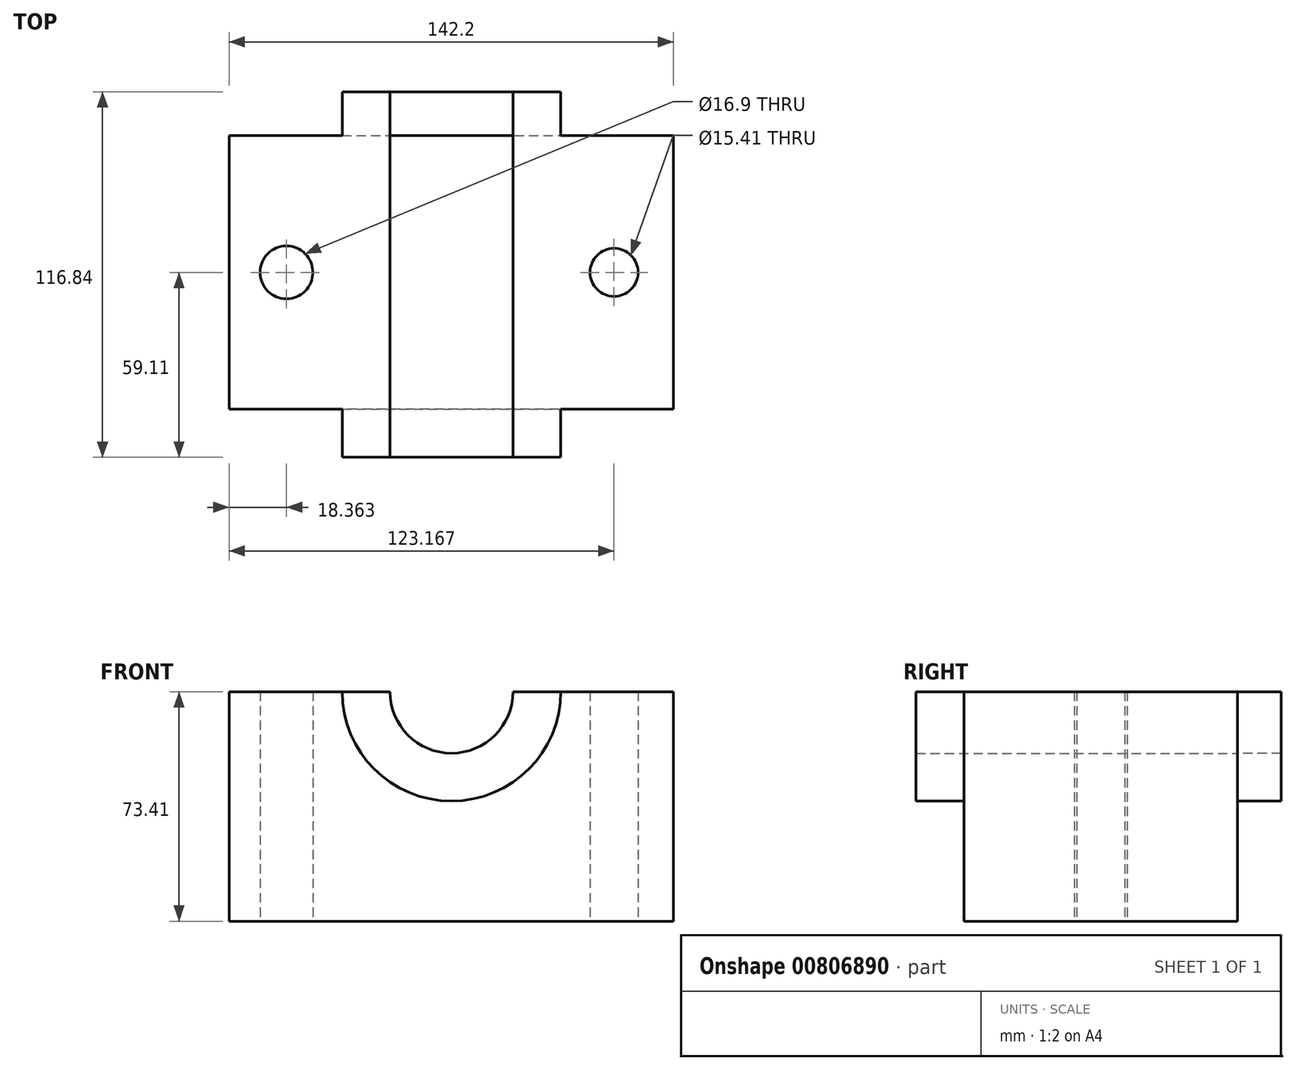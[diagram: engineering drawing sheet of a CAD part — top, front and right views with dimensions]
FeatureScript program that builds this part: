
annotation { "Feature Type Name" : "Feature", "Feature Type Description" : "" }
export const myFeature = defineFeature(function(context is Context, id is Id, definition is map)
    precondition{}
    {
        {
            var Q0;
            Q0=qCreatedBy(makeId("Top.planeOp"),FACE);
            var sketch = newSketch(context, id + "F0", { "sketchPlane" : qUnion([Q0])});
            skLineSegment(sketch, "E0.bottom", {"start": v(71.1, -43.76) * mm, "end": v(-71.1, -43.76) * mm});
            skLineSegment(sketch, "E0.top", {"start": v(71.1, 43.76) * mm, "end": v(-71.1, 43.76) * mm});
            skLineSegment(sketch, "E0.left", {"start": v(71.1, -43.76) * mm, "end": v(71.1, 43.76) * mm});
            skLineSegment(sketch, "E0.right", {"start": v(-71.1, -43.76) * mm, "end": v(-71.1, 43.76) * mm});
            skPoint(sketch, "E0.middle", {"position": v(0, 0) * mm});
            skCircle(sketch, "E1", {"center": v(-52.74, 0) * mm, "radius": 8.45 * mm});
            skPoint(sketch, "E1.centerSnap0", {"position": v(-71.1, 0) * mm});
            skCircle(sketch, "E2", {"center": v(52.07, 0) * mm, "radius": 7.7 * mm});
            skSolve(sketch);
        }
        {
            var Q0;
            Q0=makeQuery(id+"F0.imprint","IMPRINT",FACE,{"disambiguationData":[TD([[makeQuery(id+"F0.imprint","IMPRINT",EDGE,{"derivedFrom":sQuery(id+"F0.wireOp",EDGE,"E0.bottom")}),-1.0]])]});
            extrude(context, id + "F1", {"entities" : qUnion([Q0]), "depth" : 73.4 * mm, "offsetDistance" : 25.4 * mm});
        }
        {
            var Q0;
            Q0=makeQuery(id+"F1.opExtrude","SWEPT_FACE",FACE,{"disambiguationData":[OSD([sQuery(id+"F0.wireOp",EDGE,"E0.top")])]});
            var sketch = newSketch(context, id + "F2", { "sketchPlane" : qUnion([Q0])});
            skArc(sketch, "E3", {"start": v(-35.05, 73.4) * mm, "mid": v(-0.07, 38.43) * mm, "end": v(34.91, 73.4) * mm});
            skCircle(sketch, "E4", {"center": v(-0.07, 73.4) * mm, "radius": 19.68 * mm});
            skSolve(sketch);
        }
        {
            var Q0;
            {var subQ0=sQuery(id+"F2.wireOp",EDGE,"E3");Q0=makeQuery(id+"F2.imprint","IMPRINT",FACE,{"disambiguationData":[TD([[makeQuery(id+"F2.imprint","IMPRINT",EDGE,{"derivedFrom":subQ0}),1.0]])]});}
            extrude(context, id + "F3", {"entities" : qUnion([Q0]), "operationType" : NewBodyOperationType.ADD, "oppositeDirection" : true, "depth" : 102.87 * mm, "offsetDistance" : 25.4 * mm});
        }
        {
            var Q0;
            {var subQ0=sQuery(id+"F2.wireOp",EDGE,"E4");var subQ1=makeQuery(id+"F1.opExtrude","CAP_EDGE",EDGE,{"disambiguationData":[OSD([sQuery(id+"F0.wireOp",EDGE,"E0.top")])],"isStart":false});var subQ2=makeQuery(id+"F2.imprint","INTERSECT",VERTEX,{"disambiguationData":[OD(0.0)],"derivedFrom":[subQ1,subQ0]});Q0=makeQuery(id+"F2.imprint","IMPRINT",FACE,{"disambiguationData":[TD([[makeQuery(id+"F2.imprint","IMPRINT",EDGE,{"disambiguationData":[TD([[subQ2,-1.0]])],"derivedFrom":subQ0}),1.0]])]});}
            var Q1;
            {var subQ0=sQuery(id+"F2.wireOp",EDGE,"E4");var subQ1=makeQuery(id+"F1.opExtrude","CAP_EDGE",EDGE,{"disambiguationData":[OSD([sQuery(id+"F0.wireOp",EDGE,"E0.top")])],"isStart":false});var subQ2=makeQuery(id+"F2.imprint","INTERSECT",VERTEX,{"disambiguationData":[OD(0.0)],"derivedFrom":[subQ1,subQ0]});Q1=makeQuery(id+"F2.imprint","IMPRINT",FACE,{"disambiguationData":[TD([[makeQuery(id+"F2.imprint","IMPRINT",EDGE,{"disambiguationData":[TD([[subQ2,1.0]])],"derivedFrom":subQ0}),1.0]])]});}
            extrude(context, id + "F4", {"entities" : qUnion([Q0, Q1]), "operationType" : NewBodyOperationType.REMOVE, "endBound" : BoundingType.THROUGH_ALL, "oppositeDirection" : true, "depth" : 25.4 * mm, "offsetDistance" : 25.4 * mm});
        }
        {
            var Q0;
            Q0=makeQuery(id+"F3.opExtrude","CAP_FACE",FACE,{"disambiguationData":[OSD([sQuery(id+"F0.wireOp",EDGE,"E0.top"),sQuery(id+"F2.wireOp",EDGE,"E3"),sQuery(id+"F2.wireOp",EDGE,"E4")])],"isStart":false});
            var sketch = newSketch(context, id + "F5", { "sketchPlane" : qUnion([Q0])});
            skArc(sketch, "E5", {"start": v(-34.91, 73.4) * mm, "mid": v(0.07, 38.36) * mm, "end": v(35.05, 73.4) * mm});
            skLineSegment(sketch, "E6", {"start": v(-34.91, 73.4) * mm, "end": v(-19.61, 73.4) * mm});
            skLineSegment(sketch, "E7", {"start": v(19.74, 73.4) * mm, "end": v(35.05, 73.4) * mm});
            skArc(sketch, "E8", {"start": v(-19.61, 73.4) * mm, "mid": v(0.07, 53.7) * mm, "end": v(19.74, 73.4) * mm});
            skSolve(sketch);
        }
        {
            var Q0;
            Q0=makeQuery(id+"F5.imprint","IMPRINT",FACE,{"disambiguationData":[TD([[makeQuery(id+"F5.imprint","IMPRINT",EDGE,{"derivedFrom":sQuery(id+"F5.wireOp",EDGE,"E6")}),1.0]])]});
            extrude(context, id + "F6", {"entities" : qUnion([Q0]), "operationType" : NewBodyOperationType.ADD, "oppositeDirection" : true, "depth" : 116.84 * mm, "offsetDistance" : 25.4 * mm});
        }
    });
